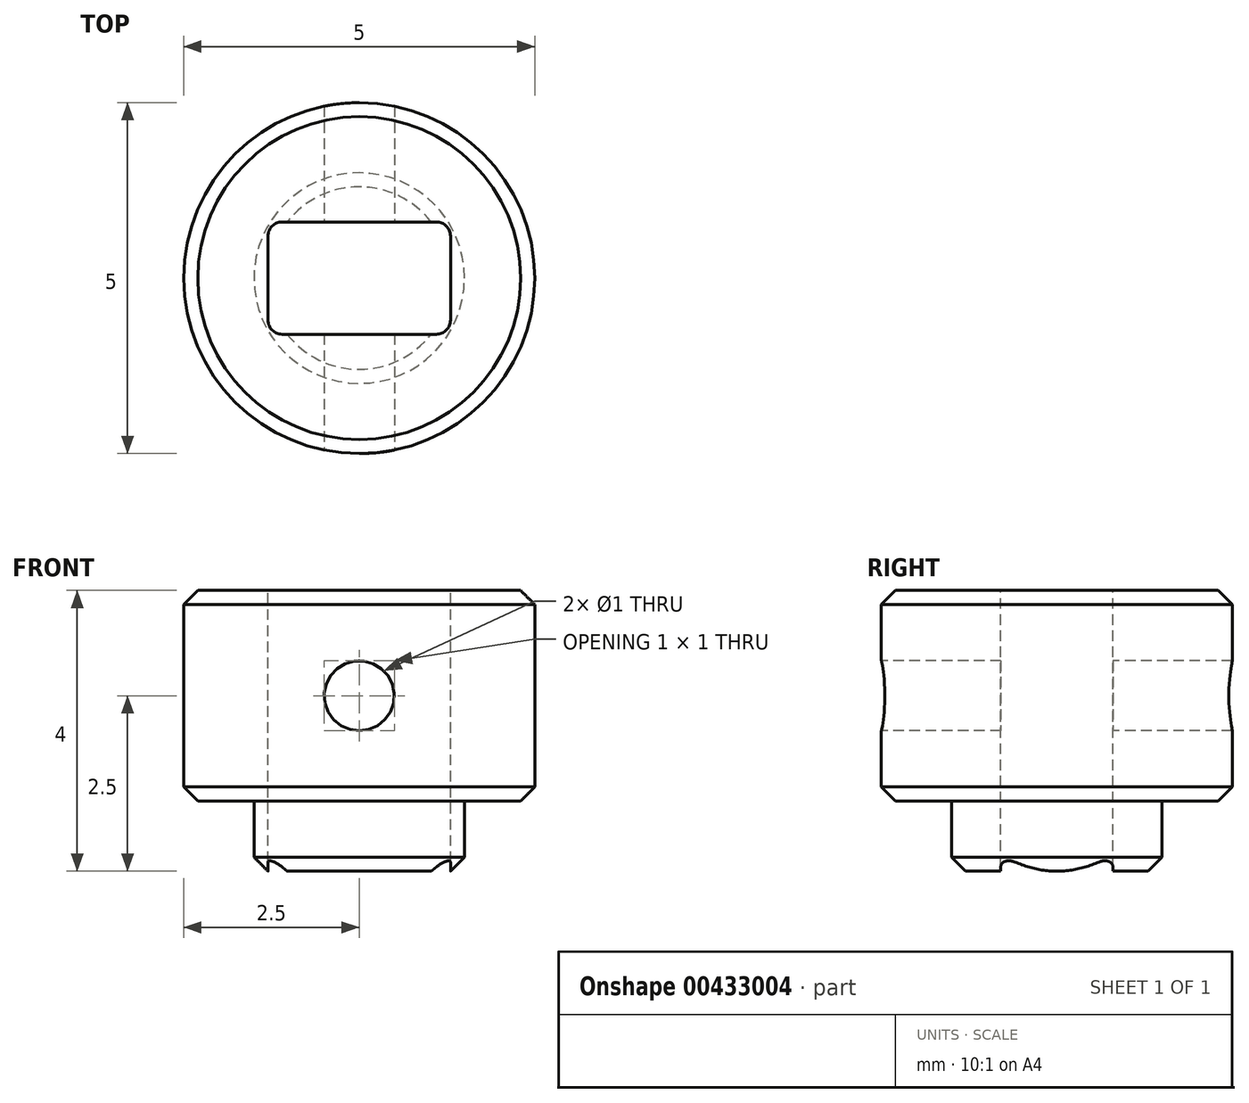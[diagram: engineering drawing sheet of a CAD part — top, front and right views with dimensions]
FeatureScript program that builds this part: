
annotation { "Feature Type Name" : "Feature", "Feature Type Description" : "" }
export const myFeature = defineFeature(function(context is Context, id is Id, definition is map)
    precondition{}
    {
        {
            var Q0;
            Q0=qCreatedBy(makeId("Top.planeOp"),FACE);
            var sketch = newSketch(context, id + "F0", { "sketchPlane" : qUnion([Q0])});
            skCircle(sketch, "E0", {"center": v(0, 0) * mm, "radius": 2.5 * mm});
            skSolve(sketch);
        }
        {
            var Q0;
            Q0=makeQuery(id+"F0.imprint","IMPRINT",FACE,{"disambiguationData":[TD([[makeQuery(id+"F0.imprint","IMPRINT",EDGE,{"derivedFrom":sQuery(id+"F0.wireOp",EDGE,"E0")}),1.0]])]});
            extrude(context, id + "F1", {"entities" : qUnion([Q0]), "depth" : 3 * mm});
        }
        {
            var Q0;
            Q0=makeQuery(id+"F1.opExtrude","CAP_FACE",FACE,{"disambiguationData":[OSD([sQuery(id+"F0.wireOp",EDGE,"E0")])],"isStart":true});
            var sketch = newSketch(context, id + "F2", { "sketchPlane" : qUnion([Q0])});
            skCircle(sketch, "E1", {"center": v(0, 0) * mm, "radius": 1.5 * mm});
            skSolve(sketch);
        }
        {
            var Q0;
            Q0=makeQuery(id+"F2.imprint","IMPRINT",FACE,{"disambiguationData":[TD([[makeQuery(id+"F2.imprint","IMPRINT",EDGE,{"derivedFrom":sQuery(id+"F2.wireOp",EDGE,"E1")}),1.0]])]});
            extrude(context, id + "F3", {"entities" : qUnion([Q0]), "operationType" : NewBodyOperationType.ADD, "depth" : 1 * mm});
        }
        {
            var Q0;
            Q0=qCreatedBy(makeId("Front.planeOp"),FACE);
            cPlane(context, id + "F4", {"entities" : qUnion([Q0]), "cplaneType" : CPlaneType.OFFSET, "offset" : 5 * mm, "width" : 150 * mm, "height" : 150 * mm});
        }
        {
            var Q0;
            Q0=qCreatedBy(id+"F4.planeOp",FACE);
            var sketch = newSketch(context, id + "F5", { "sketchPlane" : qUnion([Q0])});
            skPoint(sketch, "E2", {"position": v(0, 1.5) * mm});
            skCircle(sketch, "E3", {"center": v(0, 1.5) * mm, "radius": 0.5 * mm});
            skSolve(sketch);
        }
        {
            var Q0;
            Q0=makeQuery(id+"F5.imprint","IMPRINT",FACE,{"disambiguationData":[TD([[makeQuery(id+"F5.imprint","IMPRINT",EDGE,{"derivedFrom":sQuery(id+"F5.wireOp",EDGE,"E3")}),1.0]])]});
            var Q1;
            Q1=sQuery(id+"F5.wireOp",EDGE,"E3");
            extrude(context, id + "F6", {"entities" : qUnion([Q0]), "operationType" : NewBodyOperationType.REMOVE, "surfaceEntities" : qUnion([Q1]), "endBound" : BoundingType.THROUGH_ALL, "oppositeDirection" : true, "depth" : 25 * mm});
        }
        {
            var Q0;
            Q0=makeQuery(id+"F1.opExtrude","CAP_FACE",FACE,{"disambiguationData":[OSD([sQuery(id+"F0.wireOp",EDGE,"E0")])],"isStart":false});
            var sketch = newSketch(context, id + "F7", { "sketchPlane" : qUnion([Q0])});
            skLineSegment(sketch, "E4.bottom", {"start": v(1.3, -0.8) * mm, "end": v(-1.3, -0.8) * mm});
            skLineSegment(sketch, "E4.top", {"start": v(1.3, 0.8) * mm, "end": v(-1.3, 0.8) * mm});
            skLineSegment(sketch, "E4.left", {"start": v(1.3, -0.8) * mm, "end": v(1.3, 0.8) * mm});
            skLineSegment(sketch, "E4.right", {"start": v(-1.3, -0.8) * mm, "end": v(-1.3, 0.8) * mm});
            skPoint(sketch, "E4.middle", {"position": v(0, 0) * mm});
            skSolve(sketch);
        }
        {
            var Q0;
            Q0=makeQuery(id+"F7.imprint","IMPRINT",FACE,{"disambiguationData":[TD([[makeQuery(id+"F7.imprint","IMPRINT",EDGE,{"derivedFrom":sQuery(id+"F7.wireOp",EDGE,"E4.bottom")}),-1.0]])]});
            extrude(context, id + "F8", {"entities" : qUnion([Q0]), "operationType" : NewBodyOperationType.REMOVE, "endBound" : BoundingType.THROUGH_ALL, "oppositeDirection" : true, "depth" : 25 * mm});
        }
        {
            var Q0;
            Q0=makeQuery(id+"F8.boolean.opBoolean","COPY",EDGE,{"derivedFrom":makeQuery(id+"F8.opExtrude","SWEPT_EDGE",EDGE,{"disambiguationData":[OSD([sQuery(id+"F7.wireOp",EDGE,"E4.top"),sQuery(id+"F7.wireOp",EDGE,"E4.right")])]})});
            var Q1;
            Q1=makeQuery(id+"F8.boolean.opBoolean","COPY",EDGE,{"derivedFrom":makeQuery(id+"F8.opExtrude","SWEPT_EDGE",EDGE,{"disambiguationData":[OSD([sQuery(id+"F7.wireOp",EDGE,"E4.bottom"),sQuery(id+"F7.wireOp",EDGE,"E4.right")])]})});
            var Q2;
            Q2=makeQuery(id+"F8.boolean.opBoolean","COPY",EDGE,{"derivedFrom":makeQuery(id+"F8.opExtrude","SWEPT_EDGE",EDGE,{"disambiguationData":[OSD([sQuery(id+"F7.wireOp",EDGE,"E4.bottom"),sQuery(id+"F7.wireOp",EDGE,"E4.left")])]})});
            var Q3;
            Q3=makeQuery(id+"F8.boolean.opBoolean","COPY",EDGE,{"derivedFrom":makeQuery(id+"F8.opExtrude","SWEPT_EDGE",EDGE,{"disambiguationData":[OSD([sQuery(id+"F7.wireOp",EDGE,"E4.top"),sQuery(id+"F7.wireOp",EDGE,"E4.left")])]})});
            fillet(context, id + "F9", {"entities" : qUnion([Q0, Q1, Q2, Q3]), "radius" : 0.2 * mm, "tangentPropagation" : true, "allowEdgeOverflow" : false});
        }
        {
            var Q0;
            Q0=makeQuery(id+"F1.opExtrude","CAP_EDGE",EDGE,{"disambiguationData":[OSD([sQuery(id+"F0.wireOp",EDGE,"E0")])],"isStart":false});
            var Q1;
            Q1=makeQuery(id+"F1.opExtrude","CAP_EDGE",EDGE,{"disambiguationData":[OSD([sQuery(id+"F0.wireOp",EDGE,"E0")])],"isStart":true});
            var Q2;
            Q2=makeQuery(id+"F3.opExtrude","CAP_EDGE",EDGE,{"disambiguationData":[OSD([sQuery(id+"F2.wireOp",EDGE,"E1")])],"isStart":false});
            chamfer(context, id + "F10", {"entities" : qUnion([Q0, Q1, Q2]), "width" : 0.2 * mm, "tangentPropagation" : true});
        }
    });
